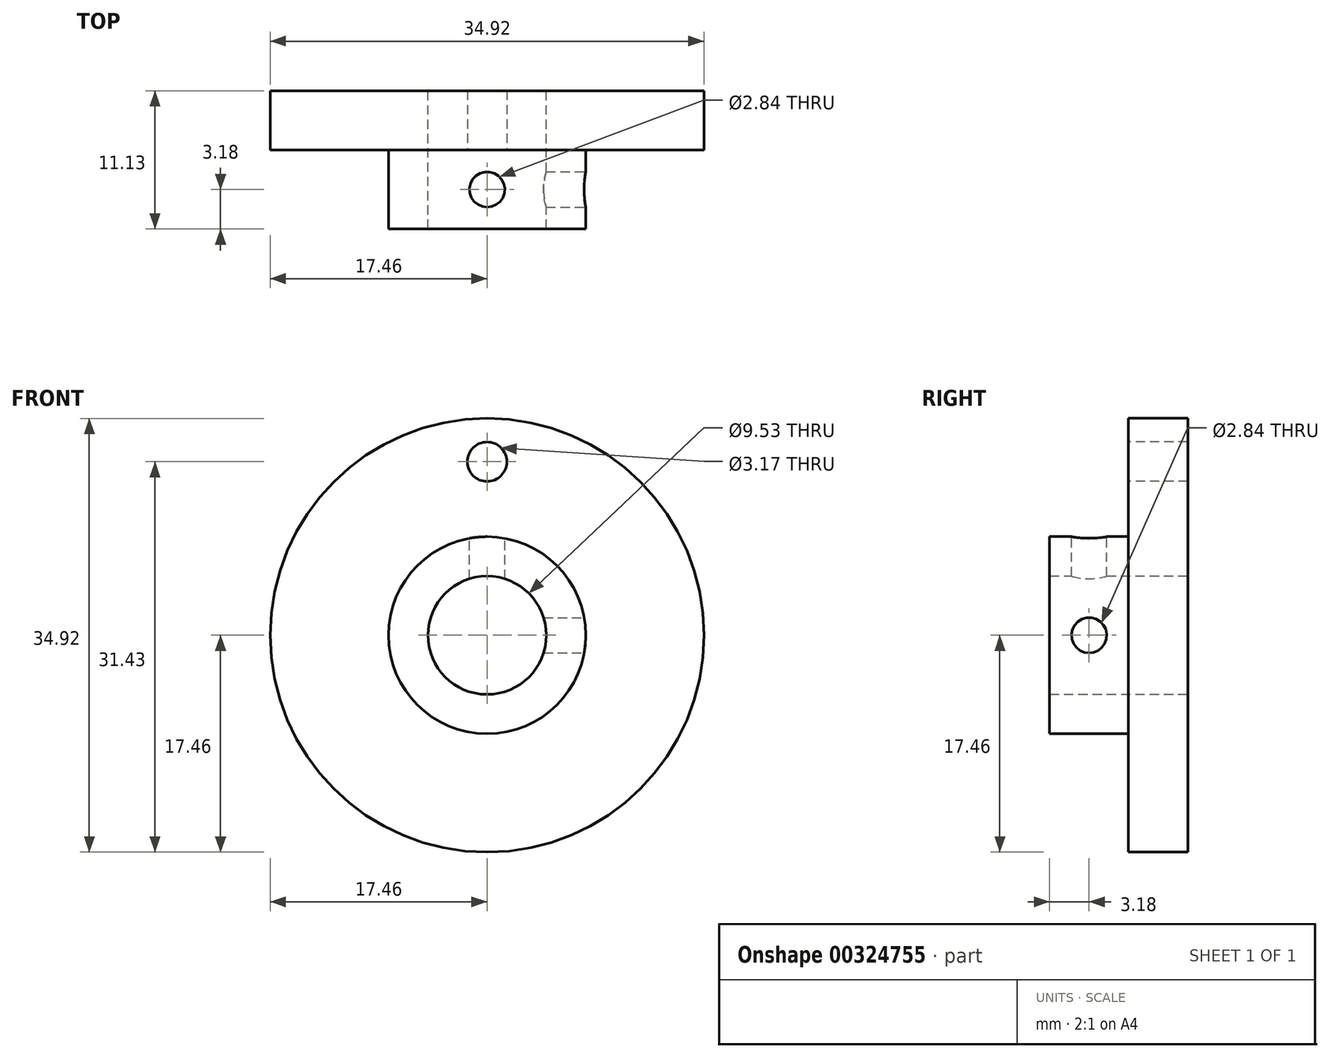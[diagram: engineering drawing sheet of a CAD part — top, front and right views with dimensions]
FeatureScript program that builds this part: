
annotation { "Feature Type Name" : "Feature", "Feature Type Description" : "" }
export const myFeature = defineFeature(function(context is Context, id is Id, definition is map)
    precondition{}
    {
        {
            var Q0;
            Q0=qCreatedBy(makeId("Front.planeOp"),FACE);
            var sketch = newSketch(context, id + "F0", { "sketchPlane" : qUnion([Q0])});
            skCircle(sketch, "E0", {"center": v(0, 0) * mm, "radius": 4.76 * mm});
            skCircle(sketch, "E1", {"center": v(0, 0) * mm, "radius": 17.46 * mm});
            skSolve(sketch);
        }
        {
            var Q0;
            Q0=makeQuery(id+"F0.imprint","IMPRINT",FACE,{"disambiguationData":[TD([[makeQuery(id+"F0.imprint","IMPRINT",EDGE,{"derivedFrom":sQuery(id+"F0.wireOp",EDGE,"E0")}),-1.0]])]});
            extrude(context, id + "F1", {"entities" : qUnion([Q0]), "depth" : 4.78 * mm, "offsetDistance" : 25.4 * mm});
        }
        {
            var Q0;
            Q0=makeQuery(id+"F1.opExtrude","CAP_FACE",FACE,{"disambiguationData":[OSD([sQuery(id+"F0.wireOp",EDGE,"E0"),sQuery(id+"F0.wireOp",EDGE,"E1")])],"isStart":false});
            var sketch = newSketch(context, id + "F2", { "sketchPlane" : qUnion([Q0])});
            skCircle(sketch, "E2", {"center": v(0, 0) * mm, "radius": 4.76 * mm});
            skCircle(sketch, "E3", {"center": v(0, 0) * mm, "radius": 7.94 * mm});
            skSolve(sketch);
        }
        {
            var Q0;
            Q0=makeQuery(id+"F2.imprint","IMPRINT",FACE,{"disambiguationData":[TD([[makeQuery(id+"F2.imprint","IMPRINT",EDGE,{"derivedFrom":sQuery(id+"F2.wireOp",EDGE,"E2")}),-1.0]])]});
            extrude(context, id + "F3", {"entities" : qUnion([Q0]), "operationType" : NewBodyOperationType.ADD, "depth" : 6.35 * mm, "offsetDistance" : 25.4 * mm});
        }
        {
            var Q0;
            Q0=makeQuery(id+"F1.opExtrude","CAP_FACE",FACE,{"disambiguationData":[OSD([sQuery(id+"F0.wireOp",EDGE,"E0"),sQuery(id+"F0.wireOp",EDGE,"E1")])],"isStart":false});
            var sketch = newSketch(context, id + "F4", { "sketchPlane" : qUnion([Q0])});
            skSolve(sketch);
        }
        {
            var Q0;
            Q0=makeQuery(id+"F4.imprint","IMPRINT",FACE,{"disambiguationData":[TD([[makeQuery(id+"F4.imprint","IMPRINT",EDGE,{"derivedFrom":makeQuery(id+"F1.opExtrude","CAP_EDGE",EDGE,{"disambiguationData":[OSD([sQuery(id+"F0.wireOp",EDGE,"E1")])],"isStart":false})}),1.0]])]});
            var sketch = newSketch(context, id + "F5", { "sketchPlane" : qUnion([Q0])});
            skCircle(sketch, "E4", {"center": v(0, 0) * mm, "radius": 13.97 * mm, "construction": true});
            skCircle(sketch, "E5", {"center": v(0, 13.97) * mm, "radius": 1.59 * mm});
            skSolve(sketch);
        }
        {
            var Q0;
            Q0=makeQuery(id+"F5.imprint","IMPRINT",FACE,{"disambiguationData":[TD([[makeQuery(id+"F5.imprint","IMPRINT",EDGE,{"derivedFrom":sQuery(id+"F5.wireOp",EDGE,"E5")}),1.0]])]});
            extrude(context, id + "F6", {"entities" : qUnion([Q0]), "operationType" : NewBodyOperationType.REMOVE, "endBound" : BoundingType.THROUGH_ALL, "oppositeDirection" : true, "depth" : 25.4 * mm, "offsetDistance" : 25.4 * mm});
        }
        {
            var Q0;
            Q0=qCreatedBy(makeId("Top.planeOp"),FACE);
            cPlane(context, id + "F7", {"entities" : qUnion([Q0]), "cplaneType" : CPlaneType.OFFSET, "offset" : 7.94 * mm, "width" : 152.4 * mm, "height" : 152.4 * mm});
        }
        {
            var Q0;
            Q0=qCreatedBy(id+"F7.planeOp",FACE);
            var sketch = newSketch(context, id + "F8", { "sketchPlane" : qUnion([Q0])});
            skCircle(sketch, "E6", {"center": v(0, -7.95) * mm, "radius": 1.42 * mm});
            skSolve(sketch);
        }
        {
            var Q0;
            Q0=makeQuery(id+"F8.imprint","IMPRINT",FACE,{"disambiguationData":[TD([[makeQuery(id+"F8.imprint","IMPRINT",EDGE,{"derivedFrom":sQuery(id+"F8.wireOp",EDGE,"E6")}),1.0]])]});
            extrude(context, id + "F9", {"entities" : qUnion([Q0]), "operationType" : NewBodyOperationType.REMOVE, "oppositeDirection" : true, "depth" : 5.08 * mm, "offsetDistance" : 25.4 * mm});
        }
        {
            var Q0;
            Q0=qCreatedBy(makeId("Right.planeOp"),FACE);
            cPlane(context, id + "F10", {"entities" : qUnion([Q0]), "cplaneType" : CPlaneType.OFFSET, "offset" : 7.94 * mm, "width" : 152.4 * mm, "height" : 152.4 * mm});
        }
        {
            var Q0;
            Q0=qCreatedBy(id+"F10.planeOp",FACE);
            var sketch = newSketch(context, id + "F11", { "sketchPlane" : qUnion([Q0])});
            skCircle(sketch, "E7", {"center": v(-7.95, 0) * mm, "radius": 1.42 * mm});
            skSolve(sketch);
        }
        {
            var Q0;
            Q0=makeQuery(id+"F11.imprint","IMPRINT",FACE,{"disambiguationData":[TD([[makeQuery(id+"F11.imprint","IMPRINT",EDGE,{"derivedFrom":sQuery(id+"F11.wireOp",EDGE,"E7")}),1.0]])]});
            extrude(context, id + "F12", {"entities" : qUnion([Q0]), "operationType" : NewBodyOperationType.REMOVE, "oppositeDirection" : true, "depth" : 5.08 * mm, "offsetDistance" : 25.4 * mm});
        }
    });
